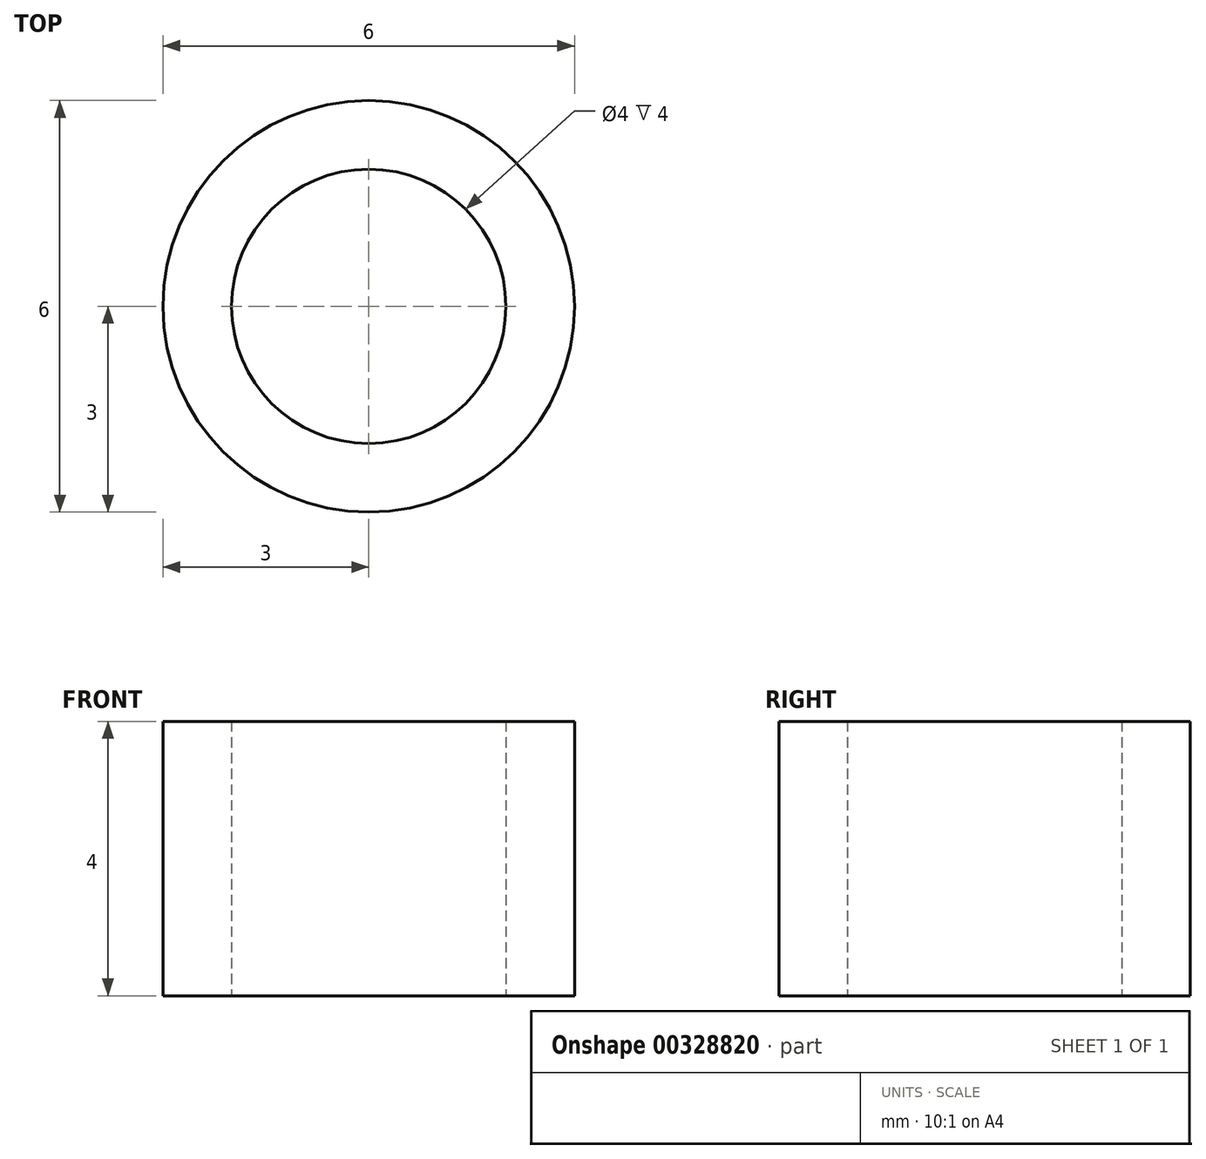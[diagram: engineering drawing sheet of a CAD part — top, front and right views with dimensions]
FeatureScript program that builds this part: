
annotation { "Feature Type Name" : "Feature", "Feature Type Description" : "" }
export const myFeature = defineFeature(function(context is Context, id is Id, definition is map)
    precondition{}
    {
        {
            var Q0;
            Q0=qCreatedBy(makeId("Top.planeOp"),FACE);
            var sketch = newSketch(context, id + "F0", { "sketchPlane" : qUnion([Q0])});
            skCircle(sketch, "E0", {"center": v(0, 0) * mm, "radius": 2 * mm});
            skCircle(sketch, "E1", {"center": v(0, 0) * mm, "radius": 3 * mm});
            skSolve(sketch);
        }
        {
            var Q0;
            Q0=makeQuery(id+"F0.imprint","IMPRINT",FACE,{"disambiguationData":[TD([[makeQuery(id+"F0.imprint","IMPRINT",EDGE,{"derivedFrom":sQuery(id+"F0.wireOp",EDGE,"E0")}),-1.0]])]});
            extrude(context, id + "F1", {"entities" : qUnion([Q0]), "depth" : 4 * mm});
        }
    });
